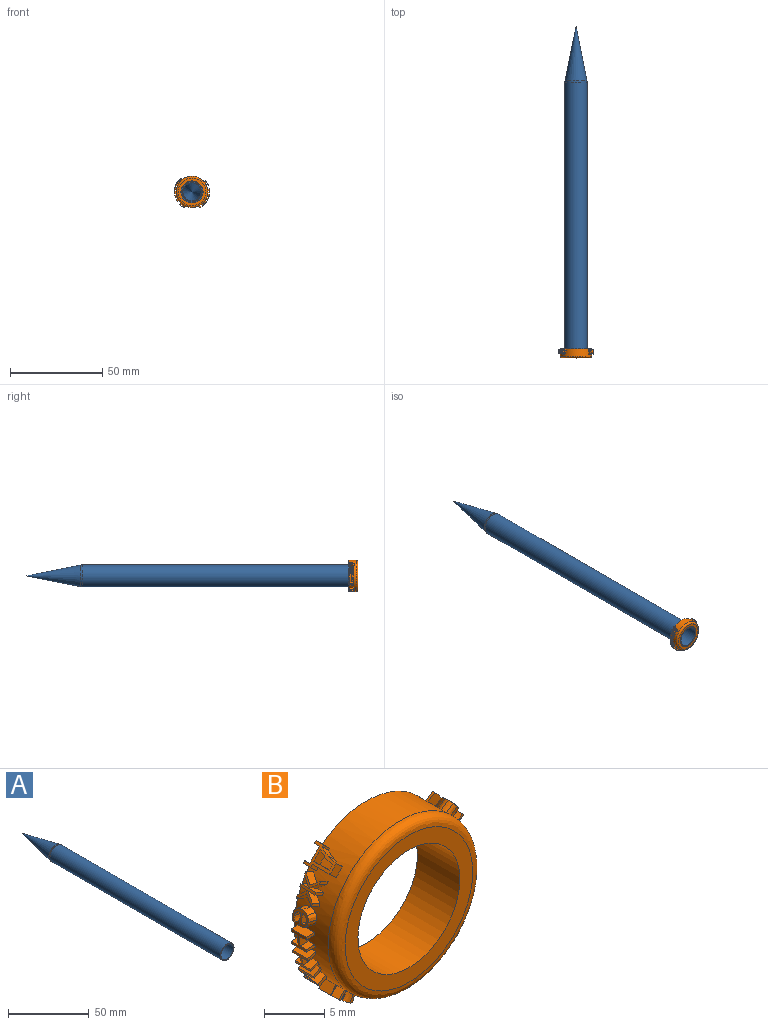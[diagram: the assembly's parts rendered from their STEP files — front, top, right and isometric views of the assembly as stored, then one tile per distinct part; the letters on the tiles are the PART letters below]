
ASSEMBLY  parts=2 mates=1
PART A: 8 faces, bbox 12x180x12 mm
  f0: cylinder r=5.5mm len=150mm, axis (0,1,0), area 5183.6mm2, adj f2,f4
  f1: cylinder r=6mm len=149.51mm, axis (0,1,0), area 5636.2mm2, adj f2,f5
  f2: plane 12x12mm, normal (0,-1,0), area 18.1mm2, adj f0,f1
  f3: cone r=6mm half-angle=11.3deg, axis (0,-1,0), area 558.2mm2, adj f5
  f4: plane 11x11mm, normal (0,-1,0), area 17.5mm2, adj f0,f6
  f5: torus R=1mm, axis (0,-1,0), area 37mm2, adj f1,f3
  f6: torus R=1mm, axis (0,-1,0), area 9.1mm2, adj f4,f7
  f7: cone r=5.02mm half-angle=11.3deg, axis (0,-1,0), area 388.1mm2, adj f6
PART B: 300 faces, bbox 19x5x17.5 mm
  f0: plane 2.34x0.87mm, normal (0.87,0,0.49), area 2.3mm2, adj f1,f9,f10,f32
  f1: plane 1.01x0.73mm, normal (0,-1,0), area 0.3mm2, adj f0,f2,f10,f32
  f2: plane 2.36x0.87mm, normal (-0.87,0,-0.49), area 2.4mm2, adj f1,f3,f10,f32
  f3: extruded ~0.92x0.56mm, area 0.3mm2, adj f2,f4,f10,f32
  f4: extruded ~1x0.7mm, area 0.3mm2, adj f3,f5,f10,f32
  f5: extruded ~1x0.7mm, area 0.2mm2, adj f4,f6,f10,f32
  f6: plane 0.88x0.49mm, normal (-0.87,0,-0.49), area 0.2mm2, adj f5,f7,f10,f32
  f7: extruded ~1x0.7mm, area 0.2mm2, adj f6,f8,f10,f32
  f8: extruded ~1.1x0.88mm, area 0.5mm2, adj f7,f9,f10,f32
  f9: extruded ~0.95x0.62mm, area 0.5mm2, adj f0,f8,f10,f32
  f10: cylinder r=9.5mm len=2.98mm, axis (0,1,0), area 0.9mm2, adj f0,f1,f2,f3,f4,f5,f6,f7
  f11: extruded ~0.95x0.86mm, area 0.3mm2, adj f12,f24,f30,f32
  f12: extruded ~0.97x0.88mm, area 0.3mm2, adj f11,f13,f30,f32
  f13: extruded ~1.18x1.13mm, area 0.7mm2, adj f12,f14,f30,f32
  f14: extruded ~0.93x0.83mm, area 0.7mm2, adj f13,f15,f30,f32
  f15: extruded ~0.92x0.82mm, area 0.7mm2, adj f14,f16,f30,f32
  f16: extruded ~1.14x1.09mm, area 0.6mm2, adj f15,f17,f30,f32
  f17: extruded ~1.12x1.06mm, area 0.6mm2, adj f16,f18,f30,f32
  f18: extruded ~0.9x0.8mm, area 0.6mm2, adj f17,f19,f30,f32
  f19: plane 0.77x0.64mm, normal (0.77,0,0.64), area 0.2mm2, adj f18,f20,f30,f32
  f20: plane 1.57x1.56mm, normal (0,1,0), area 1.2mm2, adj f19,f21,f30,f32
  f21: extruded ~0.87x0.77mm, area 0.5mm2, adj f20,f22,f30,f32
  f22: extruded ~1.04x0.97mm, area 0.5mm2, adj f21,f23,f30,f32
  f23: extruded ~1.15x1.09mm, area 0.6mm2, adj f22,f24,f30,f32
  f24: plane 0.77x0.64mm, normal (0.77,0,0.64), area 0.2mm2, adj f11,f23,f30,f32
  f25: plane 1.36x1.35mm, normal (0,-1,0), area 0.9mm2, adj f26,f29,f30,f31
  f26: extruded ~0.87x0.76mm, area 0.4mm2, adj f25,f27,f30,f31
  f27: extruded ~0.99x0.91mm, area 0.4mm2, adj f26,f28,f30,f31
  f28: extruded ~0.98x0.89mm, area 0.4mm2, adj f27,f29,f30,f31
  f29: extruded ~0.84x0.73mm, area 0.4mm2, adj f25,f28,f30,f31
  f30: cylinder r=9.5mm len=1.83mm, axis (0,1,0), area 1.2mm2, adj f11,f12,f13,f14,f15,f16,f17,f18
  f31: cylinder r=8.5mm len=0.71mm, axis (0,1,0), area 0.4mm2, adj f25,f26,f27,f28,f29
  f32: cylinder r=8.5mm len=17mm, axis (0,1,0), area 190.6mm2, adj f0,f1,f2,f3,f4,f5,f6,f7
  f33: plane 1.21x0.79mm, normal (0.61,0,0.79), area 1.2mm2, adj f32,f34,f51,f60
  f34: plane 0.91x0.78mm, normal (0,1,0), area 0.2mm2, adj f32,f33,f35,f60
  f35: plane 0.82x0.66mm, normal (-0.6,0.21,-0.77), area 0.3mm2, adj f32,f34,f36,f60
  f36: plane 0.8x0.62mm, normal (0,1,0), area 0mm2, adj f32,f35,f37,f60
  f37: extruded ~0.96x0.83mm, area 0.4mm2, adj f32,f36,f38,f60
  f38: extruded ~0.99x0.87mm, area 0.3mm2, adj f32,f37,f39,f60
  f39: extruded ~1.06x0.95mm, area 0.4mm2, adj f32,f38,f40,f60
  f40: extruded ~0.89x0.74mm, area 0.4mm2, adj f32,f39,f41,f60
  f41: extruded ~1.34x1.31mm, area 1.2mm2, adj f32,f40,f42,f60
  f42: plane 0.97x0.85mm, normal (-0.02,-1,-0.03), area 0.3mm2, adj f32,f41,f43,f60
  f43: plane 0.79x0.61mm, normal (-0.61,0,-0.79), area 0.1mm2, adj f32,f42,f44,f60
  f44: extruded ~0.85x0.68mm, area 0.3mm2, adj f32,f43,f45,f60
  f45: extruded ~0.97x0.84mm, area 0.3mm2, adj f32,f44,f46,f60
  f46: extruded ~1.11x1.01mm, area 0.5mm2, adj f32,f45,f47,f60
  f47: plane 0.85x0.67mm, normal (-0.57,0.37,-0.73), area 0.2mm2, adj f32,f46,f48,f60
  f48: extruded ~0.98x0.85mm, area 0.3mm2, adj f32,f47,f49,f60
  f49: extruded ~0.99x0.86mm, area 0.3mm2, adj f32,f48,f50,f60
  f50: extruded ~1.09x0.99mm, area 0.5mm2, adj f32,f49,f51,f60
  f51: extruded ~0.9x0.74mm, area 0.5mm2, adj f32,f33,f50,f60
  f52: extruded ~0.88x0.73mm, area 0.3mm2, adj f53,f59,f60,f61
  f53: extruded ~1.08x0.98mm, area 0.5mm2, adj f52,f54,f60,f61
  f54: plane 0.95x0.83mm, normal (0.02,1,0.03), area 0.3mm2, adj f53,f55,f60,f61
  f55: plane 0.79x0.61mm, normal (-0.61,0,-0.79), area 0.2mm2, adj f54,f56,f60,f61
  f56: extruded ~0.88x0.73mm, area 0.4mm2, adj f55,f57,f60,f61
  f57: extruded ~1.03x0.92mm, area 0.4mm2, adj f56,f58,f60,f61
  f58: extruded ~0.95x0.81mm, area 0.3mm2, adj f57,f59,f60,f61
  f59: extruded ~0.85x0.68mm, area 0.2mm2, adj f52,f58,f60,f61
  f60: cylinder r=9.5mm len=1.83mm, axis (0,1,0), area 1.2mm2, adj f33,f34,f35,f36,f37,f38,f39,f40
  f61: cylinder r=8.5mm len=0.69mm, axis (0,1,0), area 0.4mm2, adj f52,f53,f54,f55,f56,f57,f58,f59
  f62: extruded ~0.99x0.58mm, area 0.5mm2, adj f32,f63,f78,f79
  f63: extruded ~1.13x0.87mm, area 0.5mm2, adj f32,f62,f64,f79
  f64: extruded ~1.05x0.72mm, area 0.3mm2, adj f32,f63,f65,f79
  f65: extruded ~1.01x0.64mm, area 0.3mm2, adj f32,f64,f66,f79
  f66: plane 0.91x0.43mm, normal (0,-1,0), area 0mm2, adj f32,f65,f67,f79
  f67: plane 0.93x0.46mm, normal (0.42,-0.18,0.89), area 0.2mm2, adj f32,f66,f68,f79
  f68: plane 1.01x0.61mm, normal (0,-1,0), area 0.2mm2, adj f32,f67,f69,f79
  f69: plane 1.77x0.91mm, normal (-0.42,0,-0.91), area 1.8mm2, adj f32,f68,f70,f79
  f70: plane 1.04x0.66mm, normal (0,1,0), area 0.3mm2, adj f32,f69,f71,f79
  f71: plane 0.93x0.91mm, normal (0.42,0,0.91), area 0.9mm2, adj f32,f70,f72,f79
  f72: extruded ~0.97x0.54mm, area 0.5mm2, adj f32,f71,f73,f79
  f73: extruded ~1.08x0.79mm, area 0.4mm2, adj f32,f72,f74,f79
  f74: extruded ~1.05x0.71mm, area 0.3mm2, adj f32,f73,f75,f79
  f75: extruded ~0.95x0.51mm, area 0.3mm2, adj f32,f74,f76,f79
  f76: plane 1.14x0.91mm, normal (-0.42,0,-0.91), area 1.1mm2, adj f32,f75,f77,f79
  f77: plane 1x0.67mm, normal (0,1,0), area 0.3mm2, adj f32,f76,f78,f79
  f78: plane 1.15x0.91mm, normal (0.42,0,0.91), area 1.2mm2, adj f32,f62,f77,f79
  f79: cylinder r=9.5mm len=1.8mm, axis (0,1,0), area 1.1mm2, adj f62,f63,f64,f65,f66,f67,f68,f69
  f80: extruded ~1.03x0.49mm, area 0.5mm2, adj f32,f81,f96,f97
  f81: extruded ~1.1x0.68mm, area 0.5mm2, adj f32,f80,f82,f97
  f82: extruded ~1.05x0.53mm, area 0.3mm2, adj f32,f81,f83,f97
  f83: extruded ~1.03x0.43mm, area 0.3mm2, adj f32,f82,f84,f97
  f84: plane 0.98x0.21mm, normal (0,-1,0), area 0mm2, adj f32,f83,f85,f97
  f85: plane 0.99x0.24mm, normal (0.2,-0.18,0.96), area 0.2mm2, adj f32,f84,f86,f97
  f86: plane 1.04x0.41mm, normal (0,-1,0), area 0.2mm2, adj f32,f85,f87,f97
  f87: plane 1.77x0.98mm, normal (-0.2,0,-0.98), area 1.8mm2, adj f32,f86,f88,f97
  f88: plane 1.05x0.46mm, normal (0,1,0), area 0.3mm2, adj f32,f87,f89,f97
  f89: plane 0.98x0.93mm, normal (0.2,0,0.98), area 0.9mm2, adj f32,f88,f90,f97
  f90: extruded ~1.01x0.5mm, area 0.5mm2, adj f32,f89,f91,f97
  f91: extruded ~1.07x0.6mm, area 0.4mm2, adj f32,f90,f92,f97
  f92: extruded ~1.05x0.51mm, area 0.3mm2, adj f32,f91,f93,f97
  f93: extruded ~1.01x0.32mm, area 0.3mm2, adj f32,f92,f94,f97
  f94: plane 1.14x0.98mm, normal (-0.2,0,-0.98), area 1.1mm2, adj f32,f93,f95,f97
  f95: plane 1.02x0.47mm, normal (0,1,0), area 0.3mm2, adj f32,f94,f96,f97
  f96: plane 1.15x0.98mm, normal (0.2,0,0.98), area 1.2mm2, adj f32,f80,f95,f97
  f97: cylinder r=9.5mm len=1.8mm, axis (0,1,0), area 1.1mm2, adj f80,f81,f82,f83,f84,f85,f86,f87
  f98: plane 1.77x1mm, normal (-0.04,0,-1), area 1.8mm2, adj f32,f99,f101,f102
  f99: plane 1.01x0.31mm, normal (0,1,0), area 0.3mm2, adj f32,f98,f100,f102
  f100: plane 1.77x1mm, normal (0.04,0,1), area 1.8mm2, adj f32,f99,f101,f102
  f101: plane 1.01x0.31mm, normal (0,-1,0), area 0.3mm2, adj f32,f98,f100,f102
  f102: cylinder r=9.5mm len=1.77mm, axis (0,1,0), area 0.5mm2, adj f98,f99,f100,f101
  f103: extruded ~1.01x0.15mm, area 0.1mm2, adj f32,f104,f110,f111
  f104: extruded ~1x0.13mm, area 0.1mm2, adj f32,f103,f105,f111
  f105: extruded ~1x0.13mm, area 0.1mm2, adj f32,f104,f106,f111
  f106: extruded ~1.01x0.15mm, area 0.1mm2, adj f32,f105,f107,f111
  f107: extruded ~1x0.15mm, area 0.1mm2, adj f32,f106,f108,f111
  f108: extruded ~1x0.13mm, area 0.1mm2, adj f32,f107,f109,f111
  f109: extruded ~1x0.13mm, area 0.1mm2, adj f32,f108,f110,f111
  f110: extruded ~1x0.15mm, area 0.1mm2, adj f32,f103,f109,f111
  f111: cylinder r=9.5mm len=0.36mm, axis (0,1,0), area 0.1mm2, adj f103,f104,f105,f106,f107,f108,f109,f110
  f112: extruded ~1.04x0.39mm, area 0.3mm2, adj f32,f113,f125,f131
  f113: extruded ~1.04x0.42mm, area 0.3mm2, adj f32,f112,f114,f131
  f114: extruded ~1.08x0.73mm, area 0.7mm2, adj f32,f113,f115,f131
  f115: extruded ~1.04x0.66mm, area 0.7mm2, adj f32,f114,f116,f131
  f116: extruded ~1.04x0.68mm, area 0.7mm2, adj f32,f115,f117,f131
  f117: extruded ~1.08x0.68mm, area 0.6mm2, adj f32,f116,f118,f131
  f118: extruded ~1.07x0.64mm, area 0.6mm2, adj f32,f117,f119,f131
  f119: extruded ~1.03x0.58mm, area 0.6mm2, adj f32,f118,f120,f131
  f120: plane 1x0.17mm, normal (-0.12,0,0.99), area 0.2mm2, adj f32,f119,f121,f131
  f121: plane 1.33x1.16mm, normal (0,1,0), area 1.2mm2, adj f32,f120,f122,f131
  f122: extruded ~1.02x0.47mm, area 0.5mm2, adj f32,f121,f123,f131
  f123: extruded ~1.05x0.54mm, area 0.5mm2, adj f32,f122,f124,f131
  f124: extruded ~1.08x0.68mm, area 0.6mm2, adj f32,f123,f125,f131
  f125: plane 1x0.24mm, normal (-0.12,0,0.99), area 0.2mm2, adj f32,f112,f124,f131
  f126: plane 1.1x1.04mm, normal (0,-1,0), area 0.9mm2, adj f127,f130,f131,f132
  f127: extruded ~1.02x0.38mm, area 0.4mm2, adj f126,f128,f131,f132
  f128: extruded ~1.04x0.46mm, area 0.4mm2, adj f127,f129,f131,f132
  f129: extruded ~1.04x0.44mm, area 0.4mm2, adj f128,f130,f131,f132
  f130: extruded ~1.01x0.39mm, area 0.4mm2, adj f126,f129,f131,f132
  f131: cylinder r=9.5mm len=1.83mm, axis (0,1,0), area 1.2mm2, adj f112,f113,f114,f115,f116,f117,f118,f119
  f132: cylinder r=8.5mm len=0.92mm, axis (0,1,0), area 0.4mm2, adj f126,f127,f128,f129,f130
  f133: plane 1.17x1mm, normal (0.26,-0.79,-0.55), area 0.8mm2, adj f32,f134,f141,f142
  f134: plane 0.96x0.56mm, normal (0.34,0.61,-0.71), area 0.2mm2, adj f32,f133,f135,f142
  f135: extruded ~1.07x0.78mm, area 0.5mm2, adj f32,f134,f136,f142
  f136: extruded ~0.94x0.5mm, area 0.1mm2, adj f32,f135,f137,f142
  f137: extruded ~0.91x0.44mm, area 0.4mm2, adj f32,f136,f138,f142
  f138: plane 1.68x0.9mm, normal (0.43,0,-0.9), area 1.7mm2, adj f32,f137,f139,f142
  f139: plane 1.03x0.66mm, normal (0,1,0), area 0.3mm2, adj f32,f138,f140,f142
  f140: plane 2.36x0.9mm, normal (-0.43,0,0.9), area 2.4mm2, adj f32,f139,f141,f142
  f141: plane 1.01x0.63mm, normal (0,-1,0), area 0.2mm2, adj f32,f133,f140,f142
  f142: cylinder r=9.5mm len=2.36mm, axis (0,1,0), area 0.8mm2, adj f133,f134,f135,f136,f137,f138,f139,f140
  f143: plane 0.8x0.6mm, normal (-0.6,0,0.8), area 0mm2, adj f32,f144,f162,f163
  f144: plane 1.1x1.02mm, normal (-0.42,0.71,0.56), area 0.7mm2, adj f32,f143,f145,f163
  f145: extruded ~1.1x0.98mm, area 0.7mm2, adj f32,f144,f146,f163
  f146: extruded ~0.89x0.7mm, area 0.5mm2, adj f32,f145,f147,f163
  f147: extruded ~0.93x0.76mm, area 0.5mm2, adj f32,f146,f148,f163
  f148: extruded ~1.12x1.02mm, area 0.6mm2, adj f32,f147,f149,f163
  f149: extruded ~1.25x1.19mm, area 0.8mm2, adj f32,f148,f150,f163
  f150: plane 0.88x0.72mm, normal (0.47,0.61,-0.63), area 0.2mm2, adj f32,f149,f151,f163
  f151: extruded ~0.99x0.84mm, area 0.3mm2, adj f32,f150,f152,f163
  f152: extruded ~0.97x0.82mm, area 0.3mm2, adj f32,f151,f153,f163
  f153: extruded ~1x0.85mm, area 0.3mm2, adj f32,f152,f154,f163
  f154: extruded ~0.88x0.69mm, area 0.3mm2, adj f32,f153,f155,f163
  f155: extruded ~0.83x0.63mm, area 0.3mm2, adj f32,f154,f156,f163
  f156: extruded ~0.89x0.71mm, area 0.3mm2, adj f32,f155,f157,f163
  f157: extruded ~1.03x0.9mm, area 0.6mm2, adj f32,f156,f158,f163
  f158: plane 1.15x1.12mm, normal (0.42,-0.71,-0.57), area 0.9mm2, adj f32,f157,f159,f163
  f159: plane 0.81x0.6mm, normal (0.6,0,-0.8), area 0.2mm2, adj f32,f158,f160,f163
  f160: plane 1.85x1.73mm, normal (0,1,0), area 1.6mm2, adj f32,f159,f161,f163
  f161: plane 0.81x0.6mm, normal (-0.6,0,0.8), area 0.2mm2, adj f32,f160,f162,f163
  f162: plane 1.56x1.54mm, normal (0,-1,0), area 1.2mm2, adj f32,f143,f161,f163
  f163: cylinder r=9.5mm len=2.39mm, axis (0,1,0), area 1.2mm2, adj f143,f144,f145,f146,f147,f148,f149,f150
  f164: plane 0.93x0.91mm, normal (0,-1,0), area 0.3mm2, adj f32,f165,f176,f182
  f165: plane 0.86x0.72mm, normal (-0.7,0,-0.72), area 0.9mm2, adj f32,f164,f166,f182
  f166: plane 0.91x0.88mm, normal (0,1,0), area 0.3mm2, adj f32,f165,f167,f182
  f167: plane 0.72x0.7mm, normal (0.7,0,0.72), area 0.6mm2, adj f32,f166,f168,f182
  f168: plane 1.88x1.86mm, normal (0,1,0), area 1.6mm2, adj f32,f167,f169,f182
  f169: plane 0.72x0.7mm, normal (-0.7,0,-0.72), area 0.6mm2, adj f32,f168,f170,f182
  f170: plane 0.93x0.87mm, normal (0,1,0), area 0.3mm2, adj f32,f169,f171,f182
  f171: plane 0.86x0.72mm, normal (0.7,0,0.72), area 0.9mm2, adj f32,f170,f172,f182
  f172: plane 0.87x0.82mm, normal (0,-1,0), area 0.2mm2, adj f32,f171,f173,f182
  f173: extruded ~1.04x1.03mm, area 1.1mm2, adj f32,f172,f174,f182
  f174: extruded ~1.09x0.86mm, area 1.1mm2, adj f32,f173,f175,f182
  f175: plane 1.47x1.44mm, normal (0,-1,0), area 1.1mm2, adj f32,f174,f176,f182
  f176: plane 2.11x0.72mm, normal (-0.7,0,-0.72), area 2.1mm2, adj f32,f164,f175,f182
  f177: extruded ~0.94x0.86mm, area 1mm2, adj f178,f181,f182,f183
  f178: plane 1.09x1.09mm, normal (0,1,0), area 0.5mm2, adj f177,f179,f182,f183
  f179: plane 1.86x0.72mm, normal (0.7,0,0.72), area 1.9mm2, adj f178,f180,f182,f183
  f180: plane 1.51x1.49mm, normal (0,-1,0), area 1.1mm2, adj f179,f181,f182,f183
  f181: extruded ~1x0.99mm, area 1mm2, adj f177,f180,f182,f183
  f182: cylinder r=9.5mm len=2.97mm, axis (0,1,0), area 2.2mm2, adj f164,f165,f166,f167,f168,f169,f170,f171
  f183: cylinder r=8.5mm len=1.86mm, axis (0,1,0), area 1.5mm2, adj f177,f178,f179,f180,f181
  f184: plane 1.27x1.09mm, normal (-0.35,-0.65,-0.68), area 1.1mm2, adj f32,f185,f201,f202
  f185: plane 0.89x0.86mm, normal (0.46,0,0.89), area 0.9mm2, adj f32,f184,f186,f202
  f186: plane 1.01x0.68mm, normal (0,-1,0), area 0.2mm2, adj f32,f185,f187,f202
  f187: plane 0.89x0.86mm, normal (-0.46,0,-0.89), area 0.9mm2, adj f32,f186,f188,f202
  f188: plane 1.2x1.12mm, normal (0.35,-0.65,0.68), area 1.1mm2, adj f32,f187,f189,f202
  f189: plane 1x0.73mm, normal (0,-1,0), area 0.3mm2, adj f32,f188,f190,f202
  f190: plane 1.18x1.14mm, normal (-0.35,0.65,-0.67), area 1.1mm2, adj f32,f189,f191,f202
  f191: plane 1.21x1.2mm, normal (-0.34,-0.66,-0.67), area 1.2mm2, adj f32,f190,f192,f202
  f192: plane 1.01x0.75mm, normal (0,1,0), area 0.3mm2, adj f32,f191,f193,f202
  f193: plane 1.22x1.17mm, normal (0.35,0.66,0.67), area 1.2mm2, adj f32,f192,f194,f202
  f194: plane 0.9x0.89mm, normal (-0.46,0,-0.89), area 0.9mm2, adj f32,f193,f195,f202
  f195: plane 1.01x0.68mm, normal (0,1,0), area 0.2mm2, adj f32,f194,f196,f202
  f196: plane 0.9x0.89mm, normal (0.46,0,0.89), area 0.9mm2, adj f32,f195,f197,f202
  f197: plane 1.3x1.13mm, normal (-0.35,0.66,-0.67), area 1.2mm2, adj f32,f196,f198,f202
  f198: plane 1.07x0.72mm, normal (0,1,0), area 0.3mm2, adj f32,f197,f199,f202
  f199: plane 1.34x1.14mm, normal (0.34,-0.66,0.67), area 1.2mm2, adj f32,f198,f200,f202
  f200: plane 1.3x1.08mm, normal (0.35,0.65,0.67), area 1.1mm2, adj f32,f199,f201,f202
  f201: plane 1.06x0.71mm, normal (0,-1,0), area 0.3mm2, adj f32,f184,f200,f202
  f202: cylinder r=9.5mm len=2.14mm, axis (0,1,0), area 1.5mm2, adj f184,f185,f186,f187,f188,f189,f190,f191
  f203: extruded ~1.05x0.47mm, area 0.3mm2, adj f32,f204,f216,f222
  f204: extruded ~1.05x0.51mm, area 0.3mm2, adj f32,f203,f205,f222
  f205: extruded ~1.12x0.82mm, area 0.7mm2, adj f32,f204,f206,f222
  f206: extruded ~1.04x0.66mm, area 0.7mm2, adj f32,f205,f207,f222
  f207: extruded ~1.04x0.68mm, area 0.7mm2, adj f32,f206,f208,f222
  f208: extruded ~1.11x0.76mm, area 0.6mm2, adj f32,f207,f209,f222
  f209: extruded ~1.1x0.72mm, area 0.6mm2, adj f32,f208,f210,f222
  f210: extruded ~1.03x0.58mm, area 0.6mm2, adj f32,f209,f211,f222
  f211: plane 0.98x0.21mm, normal (-0.21,0,-0.98), area 0.2mm2, adj f32,f210,f212,f222
  f212: plane 1.4x1.22mm, normal (0,1,0), area 1.2mm2, adj f32,f211,f213,f222
  f213: extruded ~1.02x0.47mm, area 0.5mm2, adj f32,f212,f214,f222
  f214: extruded ~1.07x0.62mm, area 0.5mm2, adj f32,f213,f215,f222
  f215: extruded ~1.12x0.76mm, area 0.6mm2, adj f32,f214,f216,f222
  f216: plane 0.98x0.24mm, normal (-0.21,0,-0.98), area 0.2mm2, adj f32,f203,f215,f222
  f217: plane 1.17x1.11mm, normal (0,-1,0), area 0.9mm2, adj f218,f221,f222,f223
  f218: extruded ~1.02x0.38mm, area 0.4mm2, adj f217,f219,f222,f223
  f219: extruded ~1.06x0.54mm, area 0.4mm2, adj f218,f220,f222,f223
  f220: extruded ~1.05x0.52mm, area 0.4mm2, adj f219,f221,f222,f223
  f221: extruded ~1.01x0.39mm, area 0.4mm2, adj f217,f220,f222,f223
  f222: cylinder r=9.5mm len=1.83mm, axis (0,1,0), area 1.2mm2, adj f203,f204,f205,f206,f207,f208,f209,f210
  f223: cylinder r=8.5mm len=0.9mm, axis (0,1,0), area 0.4mm2, adj f217,f218,f219,f220,f221
  f224: plane 1.01x0.29mm, normal (0,1,0), area 0.3mm2, adj f32,f225,f235,f236
  f225: plane 1x0.8mm, normal (0.02,0,-1), area 0.8mm2, adj f32,f224,f226,f236
  f226: plane 1.03x1.01mm, normal (0,1,0), area 1mm2, adj f32,f225,f227,f236
  f227: plane 1x0.8mm, normal (-0.02,0,1), area 0.8mm2, adj f32,f226,f228,f236
  f228: plane 1.03x0.29mm, normal (0,1,0), area 0.3mm2, adj f32,f227,f229,f236
  f229: plane 1.77x1mm, normal (0.02,0,-1), area 1.8mm2, adj f32,f228,f230,f236
  f230: plane 1.03x0.29mm, normal (0,-1,0), area 0.3mm2, adj f32,f229,f231,f236
  f231: plane 1x0.74mm, normal (-0.02,0,1), area 0.7mm2, adj f32,f230,f232,f236
  f232: plane 1.03x1.01mm, normal (0,-1,0), area 1mm2, adj f32,f231,f233,f236
  f233: plane 1x0.74mm, normal (0.02,0,-1), area 0.7mm2, adj f32,f232,f234,f236
  f234: plane 1.01x0.29mm, normal (0,-1,0), area 0.3mm2, adj f32,f233,f235,f236
  f235: plane 1.77x1mm, normal (-0.02,0,1), area 1.8mm2, adj f32,f224,f234,f236
  f236: cylinder r=9.5mm len=1.77mm, axis (0,1,0), area 1.2mm2, adj f224,f225,f226,f227,f228,f229,f230,f231
  f237: plane 1.02x0.52mm, normal (0,1,0), area 0.3mm2, adj f32,f238,f248,f249
  f238: plane 0.97x0.8mm, normal (0.26,0,-0.97), area 0.8mm2, adj f32,f237,f239,f249
  f239: plane 1.23x1.21mm, normal (0,1,0), area 1mm2, adj f32,f238,f240,f249
  f240: plane 0.97x0.8mm, normal (-0.26,0,0.97), area 0.8mm2, adj f32,f239,f241,f249
  f241: plane 1.06x0.51mm, normal (0,1,0), area 0.3mm2, adj f32,f240,f242,f249
  f242: plane 1.77x0.97mm, normal (0.26,0,-0.97), area 1.8mm2, adj f32,f241,f243,f249
  f243: plane 1.06x0.51mm, normal (0,-1,0), area 0.3mm2, adj f32,f242,f244,f249
  f244: plane 0.97x0.74mm, normal (-0.26,0,0.97), area 0.7mm2, adj f32,f243,f245,f249
  f245: plane 1.23x1.21mm, normal (0,-1,0), area 1mm2, adj f32,f244,f246,f249
  f246: plane 0.97x0.74mm, normal (0.26,0,-0.97), area 0.7mm2, adj f32,f245,f247,f249
  f247: plane 1.02x0.52mm, normal (0,-1,0), area 0.3mm2, adj f32,f246,f248,f249
  f248: plane 1.77x0.97mm, normal (-0.26,0,0.97), area 1.8mm2, adj f32,f237,f247,f249
  f249: cylinder r=9.5mm len=1.77mm, axis (0,1,0), area 1.2mm2, adj f237,f238,f239,f240,f241,f242,f243,f244
  f250: plane 1.02x0.78mm, normal (0,1,0), area 0.3mm2, adj f32,f251,f263,f264
  f251: plane 1.5x1.34mm, normal (0.4,0.54,-0.74), area 1.8mm2, adj f32,f250,f252,f264
  f252: plane 0.88x0.49mm, normal (-0.48,-0.04,0.88), area 0.2mm2, adj f32,f251,f253,f264
  f253: plane 0.88x0.48mm, normal (-0.48,-0.02,0.88), area 0.2mm2, adj f32,f252,f254,f264
  f254: plane 1.08x0.88mm, normal (-0.48,0,0.88), area 1.1mm2, adj f32,f253,f255,f264
  f255: plane 1.02x0.69mm, normal (0,1,0), area 0.3mm2, adj f32,f254,f256,f264
  f256: plane 1.77x0.88mm, normal (0.48,0,-0.88), area 1.8mm2, adj f32,f255,f257,f264
  f257: plane 1.06x0.76mm, normal (0,-1,0), area 0.3mm2, adj f32,f256,f258,f264
  f258: plane 1.51x1.34mm, normal (-0.4,-0.54,0.74), area 1.8mm2, adj f32,f257,f259,f264
  f259: plane 0.88x0.48mm, normal (0.48,0.06,-0.88), area 0.1mm2, adj f32,f258,f260,f264
  f260: plane 0.88x0.49mm, normal (0.48,0.04,-0.88), area 0.3mm2, adj f32,f259,f261,f264
  f261: plane 1.12x0.88mm, normal (0.48,0,-0.88), area 1.1mm2, adj f32,f260,f262,f264
  f262: plane 0.99x0.71mm, normal (0,-1,0), area 0.3mm2, adj f32,f261,f263,f264
  f263: plane 1.77x0.88mm, normal (-0.48,0,0.88), area 1.8mm2, adj f32,f250,f262,f264
  f264: cylinder r=9.5mm len=1.77mm, axis (0,1,0), area 1.3mm2, adj f250,f251,f252,f253,f254,f255,f256,f257
  f265: plane 1.16x1.13mm, normal (-0.45,-0.79,0.41), area 0.8mm2, adj f32,f266,f273,f274
  f266: plane 0.84x0.78mm, normal (-0.59,0.61,0.53), area 0.2mm2, adj f32,f265,f267,f274
  f267: extruded ~1x0.96mm, area 0.5mm2, adj f32,f266,f268,f274
  f268: extruded ~0.79x0.73mm, area 0.1mm2, adj f32,f267,f269,f274
  f269: extruded ~0.75x0.68mm, area 0.4mm2, adj f32,f268,f270,f274
  f270: plane 1.68x0.74mm, normal (-0.74,0,0.67), area 1.7mm2, adj f32,f269,f271,f274
  f271: plane 0.91x0.87mm, normal (0,1,0), area 0.3mm2, adj f32,f270,f272,f274
  f272: plane 2.36x0.74mm, normal (0.74,0,-0.67), area 2.4mm2, adj f32,f271,f273,f274
  f273: plane 0.89x0.85mm, normal (0,-1,0), area 0.2mm2, adj f32,f265,f272,f274
  f274: cylinder r=9.5mm len=2.36mm, axis (0,1,0), area 0.8mm2, adj f265,f266,f267,f268,f269,f270,f271,f272
  f275: plane 0.86x0.52mm, normal (0.86,0,-0.52), area 0mm2, adj f32,f276,f294,f295
  f276: plane 1.13x0.95mm, normal (0.6,0.71,-0.36), area 0.7mm2, adj f32,f275,f277,f295
  f277: extruded ~1.11x0.93mm, area 0.7mm2, adj f32,f276,f278,f295
  f278: extruded ~0.93x0.63mm, area 0.5mm2, adj f32,f277,f279,f295
  f279: extruded ~0.96x0.69mm, area 0.5mm2, adj f32,f278,f280,f295
  f280: extruded ~1.14x0.97mm, area 0.6mm2, adj f32,f279,f281,f295
  f281: extruded ~1.25x1.14mm, area 0.8mm2, adj f32,f280,f282,f295
  f282: plane 0.94x0.64mm, normal (-0.67,0.61,0.41), area 0.2mm2, adj f32,f281,f283,f295
  f283: extruded ~1.02x0.78mm, area 0.3mm2, adj f32,f282,f284,f295
  f284: extruded ~1.01x0.76mm, area 0.3mm2, adj f32,f283,f285,f295
  f285: extruded ~1.02x0.79mm, area 0.3mm2, adj f32,f284,f286,f295
  f286: extruded ~0.92x0.62mm, area 0.3mm2, adj f32,f285,f287,f295
  f287: extruded ~0.88x0.56mm, area 0.3mm2, adj f32,f286,f288,f295
  f288: extruded ~0.93x0.64mm, area 0.3mm2, adj f32,f287,f289,f295
  f289: extruded ~1.05x0.84mm, area 0.6mm2, adj f32,f288,f290,f295
  f290: plane 1.21x1.03mm, normal (-0.61,-0.71,0.37), area 0.9mm2, adj f32,f289,f291,f295
  f291: plane 0.86x0.52mm, normal (-0.86,0,0.52), area 0.2mm2, adj f32,f290,f292,f295
  f292: plane 1.84x1.67mm, normal (0,1,0), area 1.6mm2, adj f32,f291,f293,f295
  f293: plane 0.86x0.52mm, normal (0.86,0,-0.52), area 0.2mm2, adj f32,f292,f294,f295
  f294: plane 1.57x1.47mm, normal (0,-1,0), area 1.2mm2, adj f32,f275,f293,f295
  f295: cylinder r=9.5mm len=2.39mm, axis (0,1,0), area 1.2mm2, adj f275,f276,f277,f278,f279,f280,f281,f282
  f296: plane 15.01x15.01mm, normal (0,-1,0), area 63.6mm2, adj f298,f299
  f297: plane 17x17mm, normal (0,1,0), area 113.9mm2, adj f32,f298
  f298: cylinder r=6mm len=12mm, axis (0,1,0), area 188.5mm2, adj f296,f297
  f299: bspline ~17.44x17.44mm, area 83.4mm2, adj f32,f296
PLACE A t=(-18.15,47.78,-2.6)mm fixed
PLACE B t=(-18.15,-97.22,-2.6)mm
MATE fastened B.f298 <-> A.f0  axis (0,-1,0) through (-18.15,-102.22,-2.6)mm
